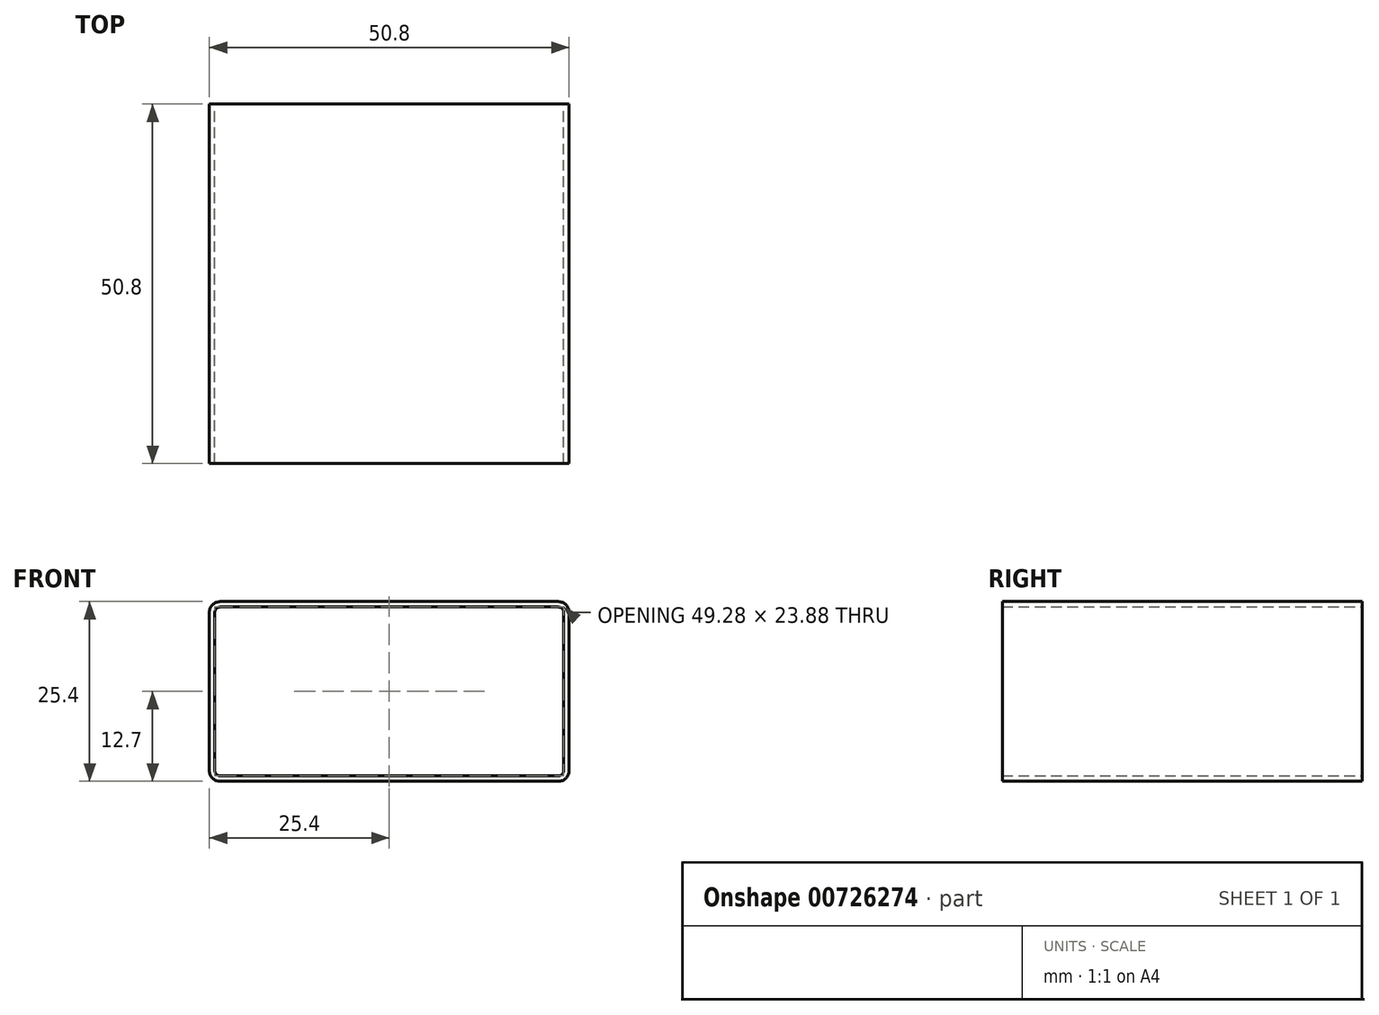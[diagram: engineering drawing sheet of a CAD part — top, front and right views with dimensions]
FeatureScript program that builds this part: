
annotation { "Feature Type Name" : "Feature", "Feature Type Description" : "" }
export const myFeature = defineFeature(function(context is Context, id is Id, definition is map)
    precondition{}
    {
        {
            var Q0;
            Q0=qCreatedBy(makeId("Front.planeOp"),FACE);
            var sketch = newSketch(context, id + "F0", { "sketchPlane" : qUnion([Q0])});
            skLineSegment(sketch, "E0.bottom", {"start": v(1.52, 0) * mm, "end": v(49.28, 0) * mm});
            skLineSegment(sketch, "E0.top", {"start": v(1.52, 25.4) * mm, "end": v(49.28, 25.4) * mm});
            skLineSegment(sketch, "E0.left", {"start": v(0, 1.52) * mm, "end": v(0, 23.88) * mm});
            skLineSegment(sketch, "E0.right", {"start": v(50.8, 1.52) * mm, "end": v(50.8, 23.88) * mm});
            skPoint(sketch, "E1.visualSharp", {"position": v(0, 25.4) * mm});
            skArc(sketch, "E1.filletArc", {"start": v(1.52, 25.4) * mm, "mid": v(0.45, 24.95) * mm, "end": v(0, 23.88) * mm});
            skPoint(sketch, "E2.visualSharp", {"position": v(0, 0) * mm});
            skArc(sketch, "E2.filletArc", {"start": v(0, 1.52) * mm, "mid": v(0.45, 0.45) * mm, "end": v(1.52, 0) * mm});
            skPoint(sketch, "E3.visualSharp", {"position": v(50.8, 0) * mm});
            skArc(sketch, "E3.filletArc", {"start": v(49.28, 0) * mm, "mid": v(50.35, 0.45) * mm, "end": v(50.8, 1.52) * mm});
            skPoint(sketch, "E4.visualSharp", {"position": v(50.8, 25.4) * mm});
            skArc(sketch, "E4.filletArc", {"start": v(50.8, 23.88) * mm, "mid": v(50.35, 24.95) * mm, "end": v(49.28, 25.4) * mm});
            skArc(sketch, "E5.0", {"start": v(1.52, 24.64) * mm, "mid": v(0.99, 24.41) * mm, "end": v(0.76, 23.88) * mm});
            skLineSegment(sketch, "E5.1", {"start": v(0.76, 1.52) * mm, "end": v(0.76, 23.88) * mm});
            skLineSegment(sketch, "E5.2", {"start": v(1.52, 24.64) * mm, "end": v(49.28, 24.64) * mm});
            skArc(sketch, "E5.3", {"start": v(0.76, 1.52) * mm, "mid": v(0.99, 0.99) * mm, "end": v(1.52, 0.76) * mm});
            skArc(sketch, "E5.4", {"start": v(50.04, 23.88) * mm, "mid": v(49.81, 24.41) * mm, "end": v(49.28, 24.64) * mm});
            skLineSegment(sketch, "E5.5", {"start": v(50.04, 1.52) * mm, "end": v(50.04, 23.88) * mm});
            skArc(sketch, "E5.6", {"start": v(49.28, 0.76) * mm, "mid": v(49.81, 0.99) * mm, "end": v(50.04, 1.52) * mm});
            skLineSegment(sketch, "E5.7", {"start": v(1.52, 0.76) * mm, "end": v(49.28, 0.76) * mm});
            skSolve(sketch);
        }
        {
            var Q0;
            Q0 = qSketchRegion(id + "F0", true);
            extrude(context, id + "F1", {"entities" : qUnion([Q0]), "depth" : 50.8 * mm, "offsetDistance" : 25.4 * mm});
        }
    });
